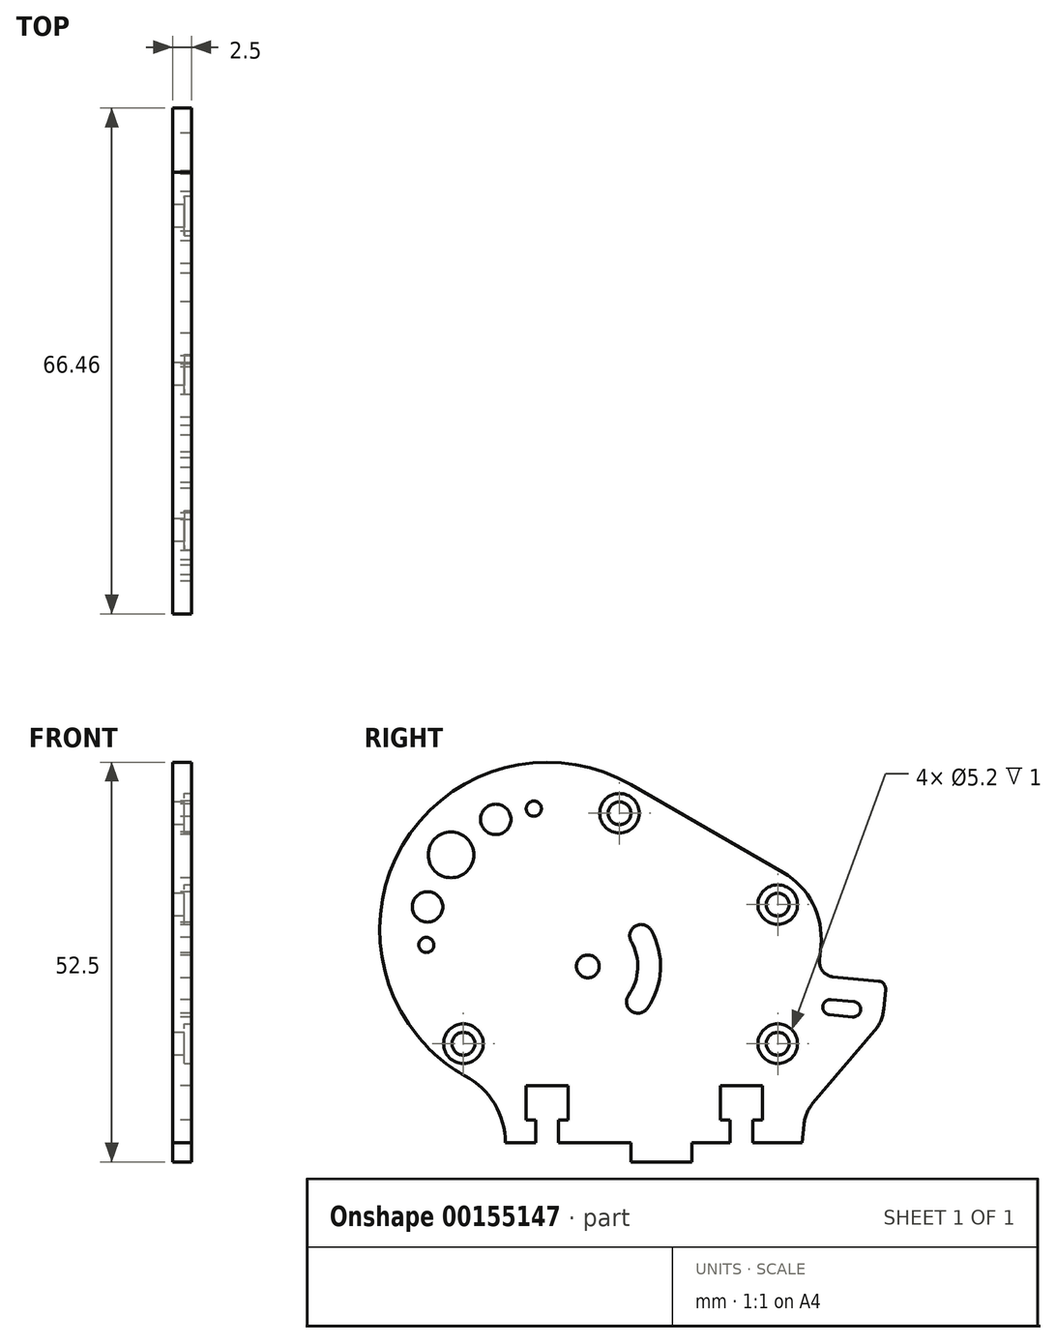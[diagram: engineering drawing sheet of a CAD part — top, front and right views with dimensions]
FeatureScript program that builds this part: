
annotation { "Feature Type Name" : "Feature", "Feature Type Description" : "" }
export const myFeature = defineFeature(function(context is Context, id is Id, definition is map)
    precondition{}
    {
        {
            var Q0;
            Q0=qCreatedBy(makeId("Right.planeOp"),FACE);
            var sketch = newSketch(context, id + "F0", { "sketchPlane" : qUnion([Q0])});
            skLineSegment(sketch, "E0.bottom", {"start": v(-19.5, 0) * mm, "end": v(-15.5, 0) * mm});
            skArc(sketch, "E1", {"start": v(-3, 47.05) * mm, "mid": v(-30.77, 42.24) * mm, "end": v(-31.02, 14.06) * mm});
            skArc(sketch, "E2", {"start": v(21.96, 25.9) * mm, "mid": v(20.89, 31.43) * mm, "end": v(17, 35.5) * mm});
            skLineSegment(sketch, "E3", {"start": v(-30.76, 13.75) * mm, "end": v(-31.02, 14.06) * mm});
            skLineSegment(sketch, "E4", {"start": v(-3, 47.05) * mm, "end": v(17, 35.5) * mm});
            skLineSegment(sketch, "E5", {"start": v(19.5, 0) * mm, "end": v(19.73, 2.43) * mm});
            skLineSegment(sketch, "E6.left", {"start": v(-15.5, 3) * mm, "end": v(-15.5, 0) * mm});
            skLineSegment(sketch, "E6.right", {"start": v(-12.5, 3) * mm, "end": v(-12.5, 0) * mm});
            skLineSegment(sketch, "E7.left", {"start": v(10, 3) * mm, "end": v(10, 0) * mm});
            skLineSegment(sketch, "E7.right", {"start": v(13, 3) * mm, "end": v(13, 0) * mm});
            skLineSegment(sketch, "E8.bottom", {"start": v(8.75, 7.5) * mm, "end": v(14.25, 7.5) * mm});
            skLineSegment(sketch, "E8.top", {"start": v(8.75, 3) * mm, "end": v(10, 3) * mm});
            skLineSegment(sketch, "E8.left", {"start": v(8.75, 7.5) * mm, "end": v(8.75, 3) * mm});
            skLineSegment(sketch, "E8.right", {"start": v(14.25, 7.5) * mm, "end": v(14.25, 3) * mm});
            skLineSegment(sketch, "E9.bottom", {"start": v(-16.75, 7.5) * mm, "end": v(-11.25, 7.5) * mm});
            skLineSegment(sketch, "E9.top", {"start": v(-16.75, 3) * mm, "end": v(-15.5, 3) * mm});
            skLineSegment(sketch, "E9.left", {"start": v(-16.75, 7.5) * mm, "end": v(-16.75, 3) * mm});
            skLineSegment(sketch, "E9.right", {"start": v(-11.25, 7.5) * mm, "end": v(-11.25, 3) * mm});
            skLineSegment(sketch, "E10.trimOffspring", {"start": v(-12.5, 3) * mm, "end": v(-11.25, 3) * mm});
            skLineSegment(sketch, "E11.trimOffspring", {"start": v(-12.5, 0) * mm, "end": v(-3, 0) * mm});
            skLineSegment(sketch, "E12.trimOffspring", {"start": v(13, 0) * mm, "end": v(19.5, 0) * mm});
            skLineSegment(sketch, "E13.trimOffspring", {"start": v(13, 3) * mm, "end": v(14.25, 3) * mm});
            skLineSegment(sketch, "E14", {"start": v(-14, 28) * mm, "end": v(0, 19.92) * mm, "construction": true});
            skLineSegment(sketch, "E15", {"start": v(-13.86, 26.19) * mm, "end": v(0, 18.19) * mm, "construction": true});
            skCircle(sketch, "E16", {"center": v(-8.66, 23.19) * mm, "radius": 1.5 * mm});
            skLineSegment(sketch, "E17.top", {"start": v(-3, -2.5) * mm, "end": v(5, -2.5) * mm});
            skLineSegment(sketch, "E17.left", {"start": v(-3, 0) * mm, "end": v(-3, -2.5) * mm});
            skLineSegment(sketch, "E17.right", {"start": v(5, 0) * mm, "end": v(5, -2.5) * mm});
            skLineSegment(sketch, "E18.trimOffspring", {"start": v(5, 0) * mm, "end": v(10, 0) * mm});
            skCircle(sketch, "E19", {"center": v(-4.5, 43.3) * mm, "radius": 1.5 * mm});
            skCircle(sketch, "E20", {"center": v(16.28, 31.3) * mm, "radius": 1.5 * mm});
            skCircle(sketch, "E21", {"center": v(-25, 13.02) * mm, "radius": 1.5 * mm});
            skCircle(sketch, "E22", {"center": v(16.28, 13.02) * mm, "radius": 1.5 * mm});
            skCircle(sketch, "E23", {"center": v(-14, 28) * mm, "radius": 16 * mm, "construction": true});
            skCircle(sketch, "E24", {"center": v(-26.62, 37.83) * mm, "radius": 3 * mm});
            skCircle(sketch, "E25", {"center": v(-20.76, 42.5) * mm, "radius": 2 * mm});
            skCircle(sketch, "E26", {"center": v(-29.72, 31) * mm, "radius": 2 * mm});
            skCircle(sketch, "E27", {"center": v(-29.87, 26) * mm, "radius": 1 * mm});
            skCircle(sketch, "E28", {"center": v(-15.76, 43.9) * mm, "radius": 1 * mm});
            skLineSegment(sketch, "E29", {"start": v(-14, 28) * mm, "end": v(-36, 28) * mm, "construction": true});
            skCircle(sketch, "E30", {"center": v(-8.66, 23.19) * mm, "radius": 8.06 * mm, "construction": true});
            skArc(sketch, "E31", {"start": v(-0.36, 27.93) * mm, "mid": v(-2.4, 28.49) * mm, "end": v(-2.96, 26.44) * mm});
            skArc(sketch, "E32", {"start": v(-3.3, 19.4) * mm, "mid": v(-2.94, 17.3) * mm, "end": v(-0.85, 17.67) * mm});
            skArc(sketch, "E33", {"start": v(-3.3, 19.4) * mm, "mid": v(-2.1, 22.87) * mm, "end": v(-2.96, 26.44) * mm});
            skArc(sketch, "E34", {"start": v(-0.85, 17.67) * mm, "mid": v(0.9, 22.73) * mm, "end": v(-0.36, 27.93) * mm});
            skLineSegment(sketch, "E35", {"start": v(-8.66, 23.19) * mm, "end": v(-1.66, 27.19) * mm, "construction": true});
            skLineSegment(sketch, "E36", {"start": v(-8.66, 23.19) * mm, "end": v(-2.08, 18.53) * mm, "construction": true});
            skLineSegment(sketch, "E37", {"start": v(23.58, 21.81) * mm, "end": v(29.55, 21.25) * mm});
            skLineSegment(sketch, "E38", {"start": v(30.45, 20.16) * mm, "end": v(30.2, 17.52) * mm});
            skLineSegment(sketch, "E39", {"start": v(29.03, 14.75) * mm, "end": v(20.9, 5.2) * mm});
            skLineSegment(sketch, "E40.trimOffspring", {"start": v(21.77, 24) * mm, "end": v(21.96, 25.9) * mm});
            skPoint(sketch, "E41.visualSharp", {"position": v(19.88, 4) * mm});
            skArc(sketch, "E41.filletArc", {"start": v(20.9, 5.2) * mm, "mid": v(20.1, 3.9) * mm, "end": v(19.73, 2.43) * mm});
            skPoint(sketch, "E42.visualSharp", {"position": v(21.59, 22) * mm});
            skArc(sketch, "E42.filletArc", {"start": v(21.77, 24) * mm, "mid": v(22.22, 22.53) * mm, "end": v(23.58, 21.81) * mm});
            skPoint(sketch, "E43.visualSharp", {"position": v(30.55, 21.15) * mm});
            skArc(sketch, "E43.filletArc", {"start": v(30.45, 20.16) * mm, "mid": v(30.23, 20.89) * mm, "end": v(29.55, 21.25) * mm});
            skPoint(sketch, "E44.visualSharp", {"position": v(30.05, 15.95) * mm});
            skArc(sketch, "E44.filletArc", {"start": v(29.03, 14.75) * mm, "mid": v(29.83, 16.04) * mm, "end": v(30.2, 17.52) * mm});
            skLineSegment(sketch, "E45", {"start": v(23.3, 18.82) * mm, "end": v(26.28, 18.54) * mm});
            skLineSegment(sketch, "E46", {"start": v(26.28, 18.54) * mm, "end": v(26.1, 16.55) * mm, "construction": true});
            skLineSegment(sketch, "E47", {"start": v(26.1, 16.55) * mm, "end": v(23.1, 16.83) * mm});
            skLineSegment(sketch, "E48", {"start": v(23.1, 16.83) * mm, "end": v(23.3, 18.82) * mm, "construction": true});
            skArc(sketch, "E49", {"start": v(23.3, 18.82) * mm, "mid": v(22.2, 17.92) * mm, "end": v(23.1, 16.83) * mm});
            skArc(sketch, "E50", {"start": v(26.1, 16.55) * mm, "mid": v(27.18, 17.45) * mm, "end": v(26.28, 18.54) * mm});
            skArc(sketch, "E51", {"start": v(-19.5, 0) * mm, "mid": v(-20.92, 5.13) * mm, "end": v(-24.76, 8.8) * mm});
            skPoint(sketch, "E52.visualSharp", {"position": v(-27.53, 9.8) * mm});
            skArc(sketch, "E52.filletArc", {"start": v(-30.76, 13.75) * mm, "mid": v(-28, 10.98) * mm, "end": v(-24.76, 8.8) * mm});
            skLineSegment(sketch, "E53", {"start": v(-8.66, 23.19) * mm, "end": v(6.34, 23.19) * mm, "construction": true});
            skSolve(sketch);
        }
        {
            var Q0;
            Q0 = qSketchRegion(id + "F0", true);
            extrude(context, id + "F1", {"entities" : qUnion([Q0]), "depth" : 2.5 * mm});
        }
        {
            var Q0;
            Q0=makeQuery(id+"F1.opExtrude","CAP_FACE",FACE,{"disambiguationData":[OSD([sQuery(id+"F0.wireOp",EDGE,"E0.bottom"),sQuery(id+"F0.wireOp",EDGE,"E1"),sQuery(id+"F0.wireOp",EDGE,"E2"),sQuery(id+"F0.wireOp",EDGE,"E3"),sQuery(id+"F0.wireOp",EDGE,"E4"),sQuery(id+"F0.wireOp",EDGE,"E5"),sQuery(id+"F0.wireOp",EDGE,"E6.left"),sQuery(id+"F0.wireOp",EDGE,"E6.right"),sQuery(id+"F0.wireOp",EDGE,"E7.left"),sQuery(id+"F0.wireOp",EDGE,"E7.right"),sQuery(id+"F0.wireOp",EDGE,"E8.bottom"),sQuery(id+"F0.wireOp",EDGE,"E8.top"),sQuery(id+"F0.wireOp",EDGE,"E8.left"),sQuery(id+"F0.wireOp",EDGE,"E8.right"),sQuery(id+"F0.wireOp",EDGE,"E9.bottom"),sQuery(id+"F0.wireOp",EDGE,"E9.top"),sQuery(id+"F0.wireOp",EDGE,"E9.left"),sQuery(id+"F0.wireOp",EDGE,"E9.right"),sQuery(id+"F0.wireOp",EDGE,"E10.trimOffspring"),sQuery(id+"F0.wireOp",EDGE,"E11.trimOffspring"),sQuery(id+"F0.wireOp",EDGE,"E12.trimOffspring"),sQuery(id+"F0.wireOp",EDGE,"E13.trimOffspring"),sQuery(id+"F0.wireOp",EDGE,"E16"),sQuery(id+"F0.wireOp",EDGE,"E17.top"),sQuery(id+"F0.wireOp",EDGE,"E17.left"),sQuery(id+"F0.wireOp",EDGE,"E17.right"),sQuery(id+"F0.wireOp",EDGE,"E18.trimOffspring"),sQuery(id+"F0.wireOp",EDGE,"E19"),sQuery(id+"F0.wireOp",EDGE,"E20"),sQuery(id+"F0.wireOp",EDGE,"E21"),sQuery(id+"F0.wireOp",EDGE,"E22"),sQuery(id+"F0.wireOp",EDGE,"E24"),sQuery(id+"F0.wireOp",EDGE,"E25"),sQuery(id+"F0.wireOp",EDGE,"E26"),sQuery(id+"F0.wireOp",EDGE,"E27"),sQuery(id+"F0.wireOp",EDGE,"E28"),sQuery(id+"F0.wireOp",EDGE,"E31"),sQuery(id+"F0.wireOp",EDGE,"E32"),sQuery(id+"F0.wireOp",EDGE,"E33"),sQuery(id+"F0.wireOp",EDGE,"E34"),sQuery(id+"F0.wireOp",EDGE,"E37"),sQuery(id+"F0.wireOp",EDGE,"E38"),sQuery(id+"F0.wireOp",EDGE,"E39"),sQuery(id+"F0.wireOp",EDGE,"E40.trimOffspring"),sQuery(id+"F0.wireOp",EDGE,"E41.filletArc"),sQuery(id+"F0.wireOp",EDGE,"E42.filletArc"),sQuery(id+"F0.wireOp",EDGE,"E43.filletArc"),sQuery(id+"F0.wireOp",EDGE,"E44.filletArc"),sQuery(id+"F0.wireOp",EDGE,"E45"),sQuery(id+"F0.wireOp",EDGE,"E47"),sQuery(id+"F0.wireOp",EDGE,"E49"),sQuery(id+"F0.wireOp",EDGE,"E50"),sQuery(id+"F0.wireOp",EDGE,"E51"),sQuery(id+"F0.wireOp",EDGE,"E52.filletArc")])],"isStart":false});
            var sketch = newSketch(context, id + "F2", { "sketchPlane" : qUnion([Q0])});
            skCircle(sketch, "E54", {"center": v(-4.5, 43.3) * mm, "radius": 2.6 * mm});
            skCircle(sketch, "E55", {"center": v(16.28, 31.3) * mm, "radius": 2.6 * mm});
            skCircle(sketch, "E56", {"center": v(16.28, 13.02) * mm, "radius": 2.6 * mm});
            skCircle(sketch, "E57", {"center": v(-25, 13.02) * mm, "radius": 2.6 * mm});
            skSolve(sketch);
        }
        {
            var Q0;
            Q0 = qSketchRegion(id + "F2", true);
            extrude(context, id + "F3", {"entities" : qUnion([Q0]), "operationType" : NewBodyOperationType.REMOVE, "oppositeDirection" : true, "depth" : 1 * mm});
        }
    });
